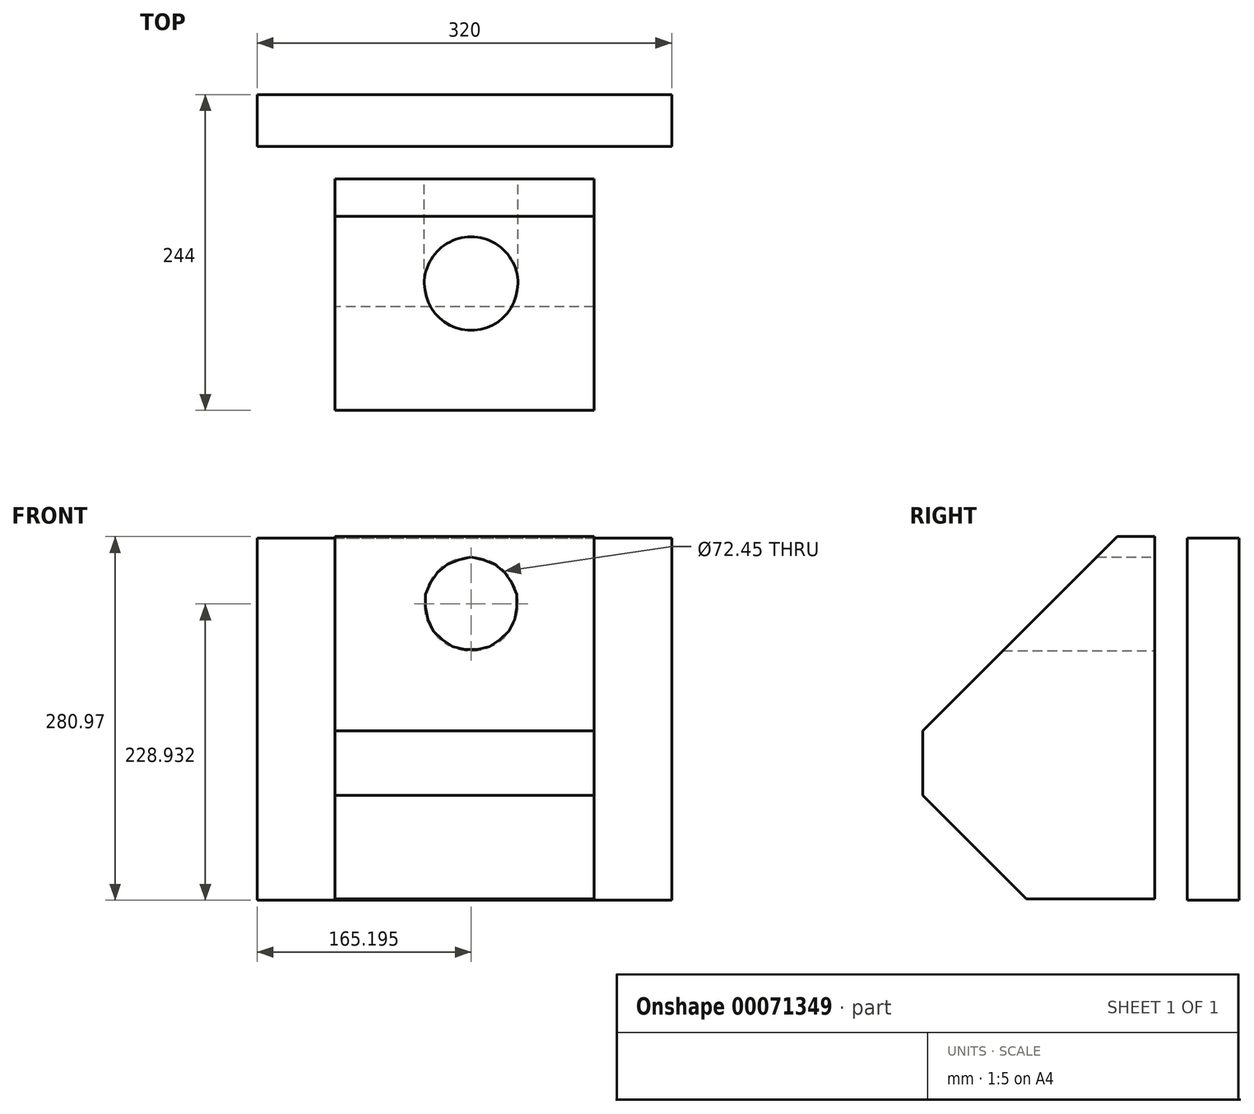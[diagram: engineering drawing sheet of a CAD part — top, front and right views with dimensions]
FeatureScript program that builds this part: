
annotation { "Feature Type Name" : "Feature", "Feature Type Description" : "" }
export const myFeature = defineFeature(function(context is Context, id is Id, definition is map)
    precondition{}
    {
        {
            var Q0;
            Q0=qCreatedBy(makeId("Front.planeOp"),FACE);
            var sketch = newSketch(context, id + "F0", { "sketchPlane" : qUnion([Q0])});
            skLineSegment(sketch, "E0.bottom", {"start": v(-159.91, -69.41) * mm, "end": v(160.09, -69.41) * mm});
            skLineSegment(sketch, "E0.top", {"start": v(-159.91, 210.59) * mm, "end": v(160.09, 210.59) * mm});
            skLineSegment(sketch, "E0.left", {"start": v(-159.91, -69.41) * mm, "end": v(-159.91, 210.59) * mm});
            skLineSegment(sketch, "E0.right", {"start": v(160.09, -69.41) * mm, "end": v(160.09, 210.59) * mm});
            skSolve(sketch);
        }
        {
            var Q0;
            Q0 = qSketchRegion(id + "F0", true);
            extrude(context, id + "F1", {"entities" : qUnion([Q0]), "depth" : 40 * mm});
        }
        {
            var Q0;
            Q0=makeQuery(id+"F1.opExtrude","CAP_FACE",FACE,{"disambiguationData":[OSD([sQuery(id+"F0.wireOp",EDGE,"E0.bottom"),sQuery(id+"F0.wireOp",EDGE,"E0.top"),sQuery(id+"F0.wireOp",EDGE,"E0.left"),sQuery(id+"F0.wireOp",EDGE,"E0.right")])],"isStart":false});
            var sketch = newSketch(context, id + "F2", { "sketchPlane" : qUnion([Q0])});
            skLineSegment(sketch, "E1.bottom", {"start": v(-99.91, 211.56) * mm, "end": v(100.09, 211.56) * mm});
            skLineSegment(sketch, "E1.top", {"start": v(-99.91, -68.44) * mm, "end": v(100.09, -68.44) * mm});
            skLineSegment(sketch, "E1.left", {"start": v(-99.91, 211.56) * mm, "end": v(-99.91, -68.44) * mm});
            skLineSegment(sketch, "E1.right", {"start": v(100.09, 211.56) * mm, "end": v(100.09, -68.44) * mm});
            skCircle(sketch, "E2", {"center": v(122.59, 133.09) * mm, "radius": 7.5 * mm});
            skCircle(sketch, "E3", {"center": v(122.59, 8.09) * mm, "radius": 7.5 * mm});
            skCircle(sketch, "E4", {"center": v(-122.41, 8.09) * mm, "radius": 7.5 * mm});
            skCircle(sketch, "E5", {"center": v(-122.41, 133.09) * mm, "radius": 7.5 * mm});
            skCircle(sketch, "E6", {"center": v(5.29, 159.52) * mm, "radius": 36.23 * mm});
            skSolve(sketch);
        }
        {
            var Q0;
            {var subQ1=sQuery(id+"F2.wireOp",EDGE,"E1.bottom");Q0=makeQuery(id+"F2.imprint","IMPRINT",FACE,{"disambiguationData":[TD([[makeQuery(id+"F2.imprint","IMPRINT",EDGE,{"derivedFrom":subQ1}),-1.0]])]});}
            var Q1;
            {var subQ0=sQuery(id+"F2.wireOp",EDGE,"E1.right");var subQ1=sQuery(id+"F2.wireOp",EDGE,"E1.top");var subQ2=makeQuery(id+"F2.imprint","INTERSECT",VERTEX,{"derivedFrom":[subQ1,subQ0]});Q1=makeQuery(id+"F2.imprint","IMPRINT",FACE,{"disambiguationData":[TD([[makeQuery(id+"F2.imprint","IMPRINT",EDGE,{"disambiguationData":[TD([[subQ2,1.0]])],"derivedFrom":subQ1}),1.0]])]});}
            extrude(context, id + "F3", {"entities" : qUnion([Q0, Q1]), "depth" : 204 * mm});
        }
        {
            var Q0;
            Q0=makeQuery(id+"F3.opExtrude","CAP_EDGE",EDGE,{"disambiguationData":[OSD([sQuery(id+"F2.wireOp",EDGE,"E1.bottom")])],"isStart":false});
            chamfer(context, id + "F4", {"entities" : qUnion([Q0]), "width" : 150 * mm, "tangentPropagation" : true});
        }
        {
            var Q0;
            Q0=makeQuery(id+"F3.opExtrude","CAP_EDGE",EDGE,{"disambiguationData":[OSD([sQuery(id+"F2.wireOp",EDGE,"E1.top")])],"isStart":false});
            chamfer(context, id + "F5", {"entities" : qUnion([Q0]), "width" : 80 * mm, "tangentPropagation" : true});
        }
        {
            var Q0;
            Q0 = qSketchRegion(id + "F2", true);
            var Q1;
            Q1=makeQuery(id+"F1.opExtrude","CAP_FACE",FACE,{"disambiguationData":[OSD([sQuery(id+"F0.wireOp",EDGE,"E0.bottom"),sQuery(id+"F0.wireOp",EDGE,"E0.top"),sQuery(id+"F0.wireOp",EDGE,"E0.left"),sQuery(id+"F0.wireOp",EDGE,"E0.right")])],"isStart":false});
            extrude(context, id + "F6", {"entities" : qUnion([Q0, Q1]), "operationType" : NewBodyOperationType.REMOVE, "depth" : 25 * mm});
        }
    });
